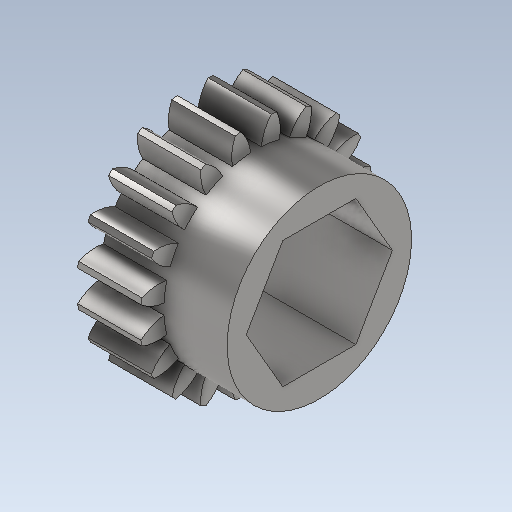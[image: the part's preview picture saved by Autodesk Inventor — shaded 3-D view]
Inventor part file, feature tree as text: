
AUTODESK INVENTOR PART (.ipt)
format: ipt  version: 2023 (Build 270158000, 158)  size: 678,400 bytes
history: native  units: in
note: dims shown in document units (in); Inventor stores cm internally (conversion verified against a paired STEP export)
features: sketch x3, other x1, revolve x1, extrude x1, hole x1, projected_geometry x1
ambient origin geometry x8: Origin, YZ Plane, XZ Plane, XY Plane, X Axis, Y Axis, Z Axis, Center Point
bodies: Solid1 (feature_tree)
feature tree (8):
  other  "TeethCuts"
  revolve  "Revolution1"  [1 undecoded]
  extrude  "Extrusion3"  Depth=0.1875in
  hole  "Hole1"  [1 undecoded]
  sketch  "Sketch3"  dims[d7=0.1875in d8=0.125in]
  sketch  "Sketch4"  dims[d9=0.1875in d10=0.1875in]
  projected_geometry  "Projected Loop1"
  sketch  "Sketch5"  dims[d12=2.4724in d13=0.13in d14=0.328in d15=0.375in d16=0.25in d17=0.5635in d18=1.0in d19=0.8108in d20=0.375in d21=0.0in d22=0.0in]
note: 2 required parameter values undecoded (feature->parameter linkage not recoverable at this tier; creation-order binding heuristic only, values carry confidence <= 0.55)